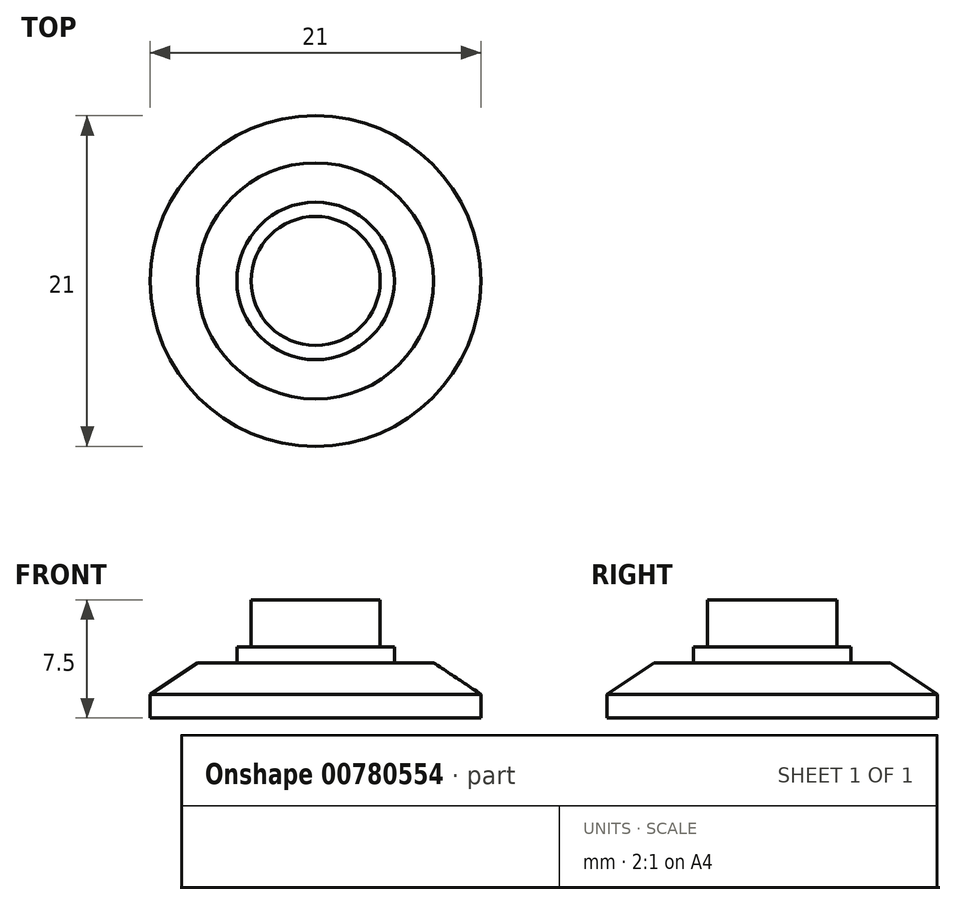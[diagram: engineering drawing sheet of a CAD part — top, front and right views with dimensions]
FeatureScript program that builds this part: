
annotation { "Feature Type Name" : "Feature", "Feature Type Description" : "" }
export const myFeature = defineFeature(function(context is Context, id is Id, definition is map)
    precondition{}
    {
        {
            var Q0;
            Q0=qCreatedBy(makeId("Top.planeOp"),FACE);
            var sketch = newSketch(context, id + "F0", { "sketchPlane" : qUnion([Q0])});
            skCircle(sketch, "E0", {"center": v(0, 0) * mm, "radius": 10.5 * mm});
            skSolve(sketch);
        }
        {
            var Q0;
            Q0=qSketchRegion(id+"F0",true);
            extrude(context, id + "F1", {"entities" : qUnion([Q0]), "depth" : 3.5 * mm, "offsetDistance" : 25 * mm});
        }
        {
            var Q0;
            Q0=makeQuery(id+"F1.opExtrude","CAP_FACE",FACE,{"disambiguationData":[OSD([sQuery(id+"F0.wireOp",EDGE,"E0")])],"isStart":false});
            var sketch = newSketch(context, id + "F2", { "sketchPlane" : qUnion([Q0])});
            skCircle(sketch, "E1", {"center": v(0, 0) * mm, "radius": 5 * mm});
            skSolve(sketch);
        }
        {
            var Q0;
            Q0=qSketchRegion(id+"F2",true);
            extrude(context, id + "F3", {"entities" : qUnion([Q0]), "operationType" : NewBodyOperationType.ADD, "depth" : 1 * mm, "offsetDistance" : 25 * mm});
        }
        {
            var Q0;
            Q0=makeQuery(id+"F3.opExtrude","CAP_FACE",FACE,{"disambiguationData":[OSD([sQuery(id+"F2.wireOp",EDGE,"E1")])],"isStart":false});
            var sketch = newSketch(context, id + "F4", { "sketchPlane" : qUnion([Q0])});
            skCircle(sketch, "E2", {"center": v(0, 0) * mm, "radius": 4.1 * mm});
            skSolve(sketch);
        }
        {
            var Q0;
            Q0=qSketchRegion(id+"F4",true);
            extrude(context, id + "F5", {"entities" : qUnion([Q0]), "operationType" : NewBodyOperationType.ADD, "depth" : 3 * mm, "offsetDistance" : 25 * mm});
        }
        {
            var Q0;
            Q0=makeQuery(id+"F1.opExtrude","CAP_EDGE",EDGE,{"disambiguationData":[OSD([sQuery(id+"F0.wireOp",EDGE,"E0")])],"isStart":false});
            chamfer(context, id + "F6", {"entities" : qUnion([Q0]), "chamferType" : ChamferType.TWO_OFFSETS, "width1" : 3 * mm, "oppositeDirection" : false, "width2" : 2 * mm, "tangentPropagation" : true});
        }
    });
